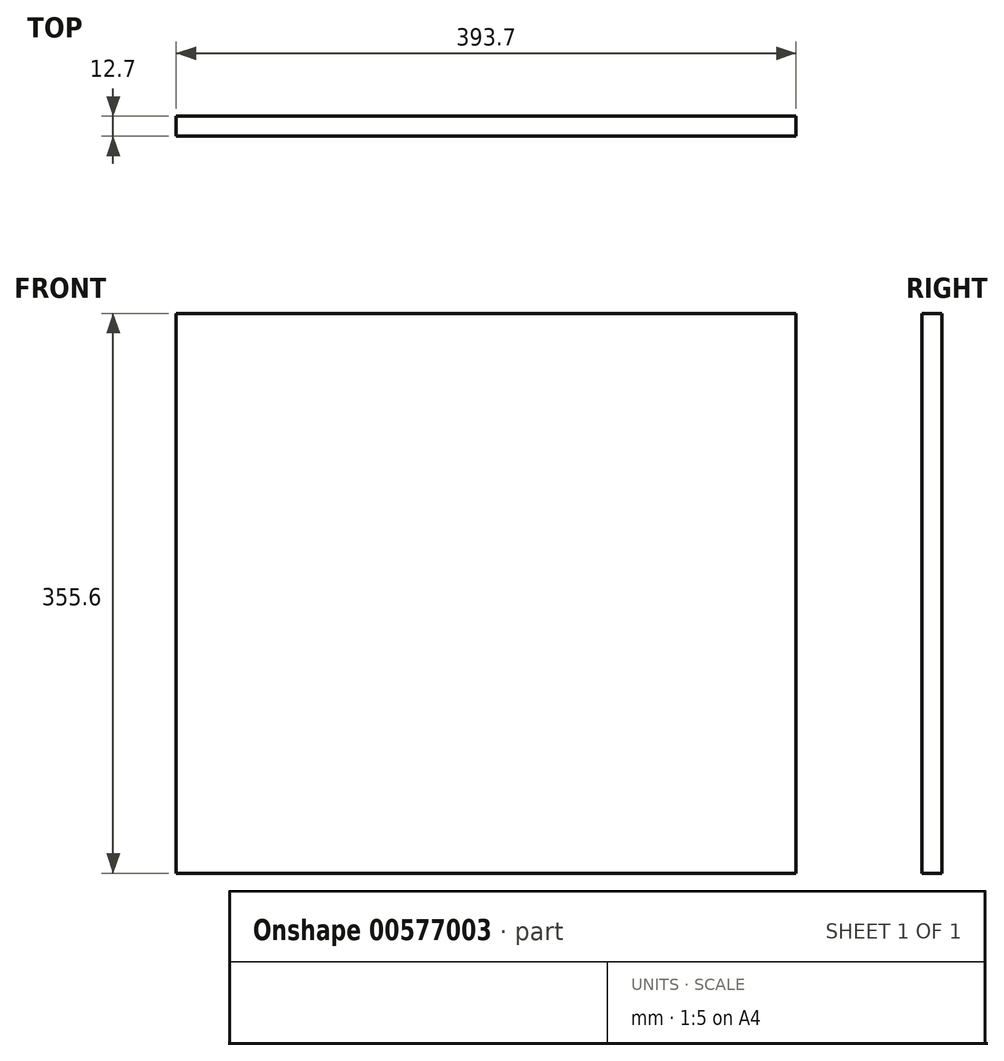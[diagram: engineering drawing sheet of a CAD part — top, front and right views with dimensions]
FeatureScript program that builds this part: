
annotation { "Feature Type Name" : "Feature", "Feature Type Description" : "" }
export const myFeature = defineFeature(function(context is Context, id is Id, definition is map)
    precondition{}
    {
        {
            var Q0;
            Q0=qCreatedBy(makeId("Front.planeOp"),FACE);
            var sketch = newSketch(context, id + "F0", { "sketchPlane" : qUnion([Q0])});
            skLineSegment(sketch, "E0.bottom", {"start": v(-196.85, 177.8) * mm, "end": v(196.85, 177.8) * mm});
            skLineSegment(sketch, "E0.top", {"start": v(-196.85, -177.8) * mm, "end": v(196.85, -177.8) * mm});
            skLineSegment(sketch, "E0.left", {"start": v(-196.85, 177.8) * mm, "end": v(-196.85, -177.8) * mm});
            skLineSegment(sketch, "E0.right", {"start": v(196.85, 177.8) * mm, "end": v(196.85, -177.8) * mm});
            skPoint(sketch, "E0.middle", {"position": v(0, 0) * mm});
            skSolve(sketch);
        }
        {
            var Q0;
            Q0 = qSketchRegion(id + "F0", true);
            extrude(context, id + "F1", {"entities" : qUnion([Q0]), "endBound" : BoundingType.SYMMETRIC, "depth" : 12.7 * mm, "offsetDistance" : 25.4 * mm});
        }
    });
